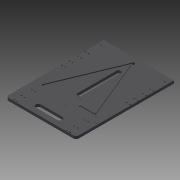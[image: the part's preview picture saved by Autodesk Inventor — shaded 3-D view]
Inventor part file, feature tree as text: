
AUTODESK INVENTOR PART (.ipt)
format: ipt  version: 2013 (Build 170138000, 138)  size: 348,160 bytes
history: native  units: mm
features: reference x11, sketch x10, extrude x9, fillet x5, hole x1
ambient origin geometry x8: Origin, YZ Plane, XZ Plane, XY Plane, X Axis, Y Axis, Z Axis, Center Point
bodies: Solid1 (feature_tree)
feature tree (36):
  extrude  "Extrusion1"  Depth=462.5mm
  fillet  "Fillet1"  Radius=12.5mm
  extrude  "Extrusion6"  Depth=87.5mm
  fillet  "Fillet2"  Radius=200.0mm
  extrude  "Extrusion7"  Depth=10.0mm TaperAngle=0.0deg
  extrude  "Extrusion17"  TaperAngle=0.0deg  [1 undecoded]
  extrude  "Extrusion18"  Depth=5.0mm
  extrude  "Extrusion19"  Depth=9.525mm
  fillet  "Fillet14"  Radius=10.0mm
  extrude  "Extrusion20"  Depth=4.0mm TaperAngle=0.0deg
  extrude  "Extrusion21"  Depth=5.0mm
  hole  "Hole1"  [1 undecoded]
  extrude  "Extrusion22"  Depth=25.0mm
  fillet  "Fillet15"  Radius=125.0mm
  fillet  "Fillet17"  Radius=25.0mm
  sketch  "Sketch1"  dims[d0=331.0mm d2=462.5mm d3=12.5mm d4=0.0mm]
  sketch  "Sketch6"  dims[d10=12.5mm d29=87.5mm d30=200.0mm]
  sketch  "Sketch7"  dims[d31=20.0mm d32=10.0mm d33=0.0mm]
  sketch  "Sketch17"  dims[d34=3.0mm d35=0.0mm]
  reference  "Reference27"
  reference  "Reference28"
  sketch  "Sketch18"  dims[d36=3.1mm d38=5.0mm]
  sketch  "Sketch19"  dims[d39=10.0mm d40=0.0mm d84=9.525mm d86=10.0mm d87=0.0mm]
  reference  "Reference29"
  sketch  "Sketch20"  dims[d88=25.0mm d89=4.0mm d90=0.0mm]
  sketch  "Sketch21"  dims[d91=4.0mm d92=0.0mm d94=5.0mm]
  reference  "Reference30"
  reference  "Reference31"
  reference  "Reference32"
  reference  "Reference33"
  reference  "Reference34"
  reference  "Reference35"
  sketch  "Sketch22"  dims[d95=4.0mm d96=0.0mm d97=10.0mm d98=0.0mm]
  reference  "Reference36"
  reference  "Reference37"
  sketch  "Sketch23"  dims[d99=3.4mm d100=6.0mm d101=6.5mm d102=3.0mm d103=90.0deg d104=8.0mm d105=20.594885mm d106=25.0mm d107=125.0mm d108=25.0mm d109=10.0mm d110=0.0mm d111=12.5mm d113=3.0mm]
note: 2 required parameter values undecoded (feature->parameter linkage not recoverable at this tier; creation-order binding heuristic only, values carry confidence <= 0.55)
